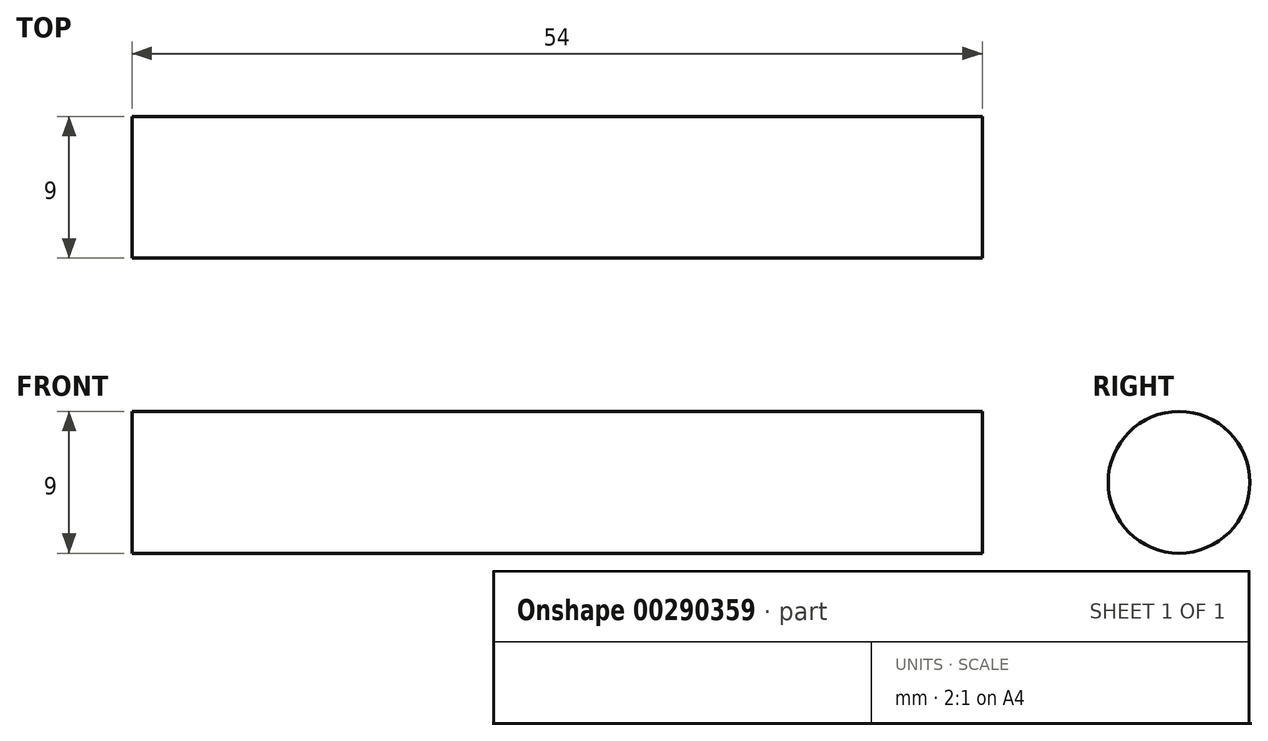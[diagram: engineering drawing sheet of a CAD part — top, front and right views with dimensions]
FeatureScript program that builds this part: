
annotation { "Feature Type Name" : "Feature", "Feature Type Description" : "" }
export const myFeature = defineFeature(function(context is Context, id is Id, definition is map)
    precondition{}
    {
        {
            var Q0;
            Q0=qCreatedBy(makeId("Front.planeOp"),FACE);
            var sketch = newSketch(context, id + "F0", { "sketchPlane" : qUnion([Q0])});
            skLineSegment(sketch, "E0", {"start": v(-15.34, 0) * mm, "end": v(-15.34, 4.5) * mm});
            skLineSegment(sketch, "E1", {"start": v(-15.34, 4.5) * mm, "end": v(38.66, 4.5) * mm});
            skLineSegment(sketch, "E2", {"start": v(38.66, 4.5) * mm, "end": v(38.66, 0) * mm});
            skLineSegment(sketch, "E3", {"start": v(38.66, 0) * mm, "end": v(-15.34, 0) * mm});
            skSolve(sketch);
        }
        {
            var Q0;
            Q0 = qSketchRegion(id + "F0", true);
            var Q1;
            Q1=sQuery(id+"F0.wireOp",EDGE,"E3");
            revolve(context, id + "F1", {"entities" : qUnion([Q0]), "axis" : qUnion([Q1]), "revolveType" : RevolveType.FULL});
        }
    });
